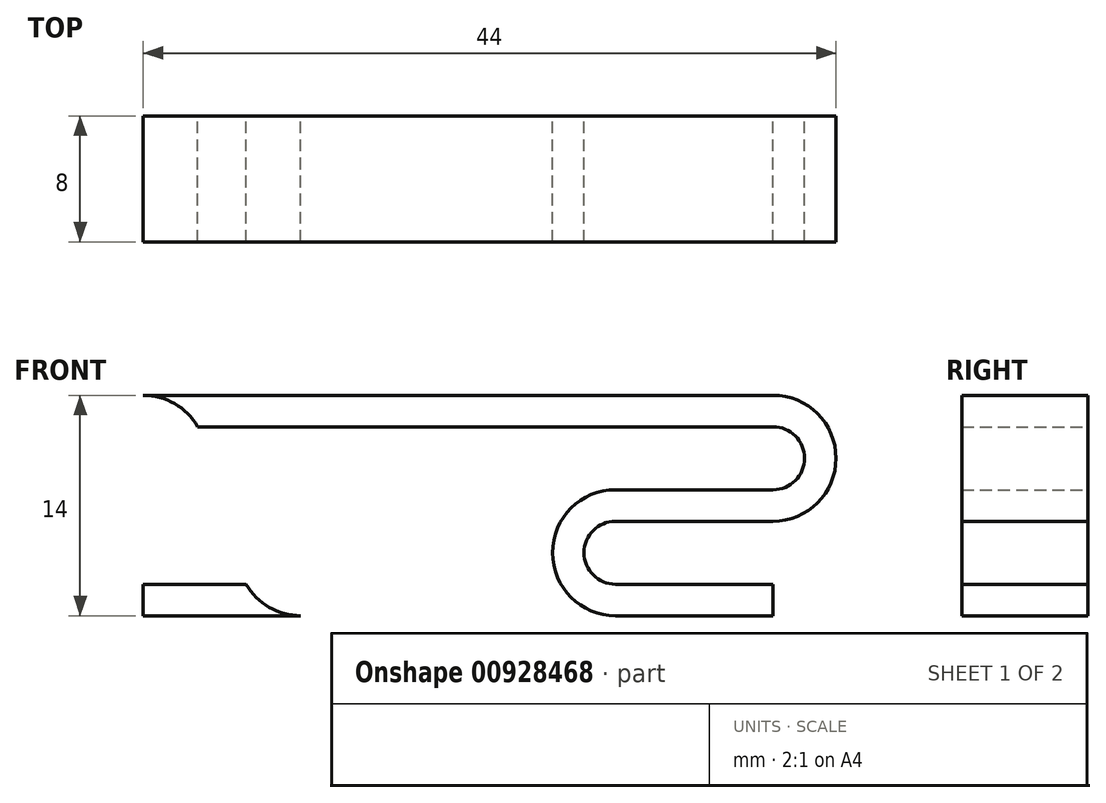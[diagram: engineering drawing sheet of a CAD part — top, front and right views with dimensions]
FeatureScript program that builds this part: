
annotation { "Feature Type Name" : "Feature", "Feature Type Description" : "" }
export const myFeature = defineFeature(function(context is Context, id is Id, definition is map)
    precondition{}
    {
        {
            var Q0;
            Q0=qCreatedBy(makeId("Front.planeOp"),FACE);
            var sketch = newSketch(context, id + "F0", { "sketchPlane" : qUnion([Q0])});
            skLineSegment(sketch, "E0", {"start": v(0, 0) * mm, "end": v(10, 0) * mm});
            skLineSegment(sketch, "E1", {"start": v(10, 0) * mm, "end": v(10, 2) * mm});
            skLineSegment(sketch, "E2", {"start": v(10, 2) * mm, "end": v(0, 2) * mm});
            skPoint(sketch, "E3", {"position": v(0, 4) * mm});
            skArc(sketch, "E4", {"start": v(0, 6) * mm, "mid": v(-2, 4) * mm, "end": v(0, 2) * mm});
            skLineSegment(sketch, "E5", {"start": v(0, 6) * mm, "end": v(10, 6) * mm});
            skPoint(sketch, "E6", {"position": v(10, 10) * mm});
            skArc(sketch, "E7", {"start": v(3.46, 6) * mm, "mid": v(-4, 4) * mm, "end": v(3.46, 2) * mm});
            skArc(sketch, "E8", {"start": v(6.54, 8) * mm, "mid": v(14, 10) * mm, "end": v(6.54, 12) * mm});
            skArc(sketch, "E9", {"start": v(10, 8) * mm, "mid": v(12, 10) * mm, "end": v(10, 12) * mm});
            skLineSegment(sketch, "E10", {"start": v(0, 8) * mm, "end": v(10, 8) * mm});
            skLineSegment(sketch, "E11", {"start": v(10, 12) * mm, "end": v(0, 12) * mm});
            skLineSegment(sketch, "E12", {"start": v(0, 12) * mm, "end": v(0, 14) * mm});
            skLineSegment(sketch, "E13", {"start": v(0, 14) * mm, "end": v(10, 14) * mm});
            skPoint(sketch, "E14", {"position": v(-4, 14) * mm});
            skPoint(sketch, "E14.positionSnap0", {"position": v(-4, 4) * mm});
            skPoint(sketch, "E15", {"position": v(-10, 14) * mm});
            skLineSegment(sketch, "E16", {"start": v(-10, 14) * mm, "end": v(-10, 0) * mm});
            skPoint(sketch, "E17.MirrorP", {"position": v(-16, 14) * mm});
            skPoint(sketch, "E18.MirrorP", {"position": v(-16, 4) * mm});
            skArc(sketch, "E19.MirrorCS", {"start": v(-23.46, 6) * mm, "mid": v(-16, 4) * mm, "end": v(-23.46, 2) * mm});
            skLineSegment(sketch, "E20.MirrorCS", {"start": v(-20, 6) * mm, "end": v(-30, 6) * mm});
            skArc(sketch, "E21.MirrorCS", {"start": v(-26.54, 8) * mm, "mid": v(-34, 10) * mm, "end": v(-26.54, 12) * mm});
            skArc(sketch, "E22.MirrorCS", {"start": v(-20, 6) * mm, "mid": v(-18, 4) * mm, "end": v(-20, 2) * mm});
            skLineSegment(sketch, "E23.MirrorCS", {"start": v(-20, 8) * mm, "end": v(-30, 8) * mm});
            skLineSegment(sketch, "E24.MirrorCS", {"start": v(-30, 0) * mm, "end": v(-30, 2) * mm});
            skLineSegment(sketch, "E25.MirrorCS", {"start": v(-30, 12) * mm, "end": v(-20, 12) * mm});
            skLineSegment(sketch, "E26.MirrorCS", {"start": v(-20, 14) * mm, "end": v(-30, 14) * mm});
            skArc(sketch, "E27.MirrorCS", {"start": v(-30, 8) * mm, "mid": v(-32, 10) * mm, "end": v(-30, 12) * mm});
            skLineSegment(sketch, "E28.MirrorCS", {"start": v(-30, 2) * mm, "end": v(-20, 2) * mm});
            skLineSegment(sketch, "E29.MirrorCS", {"start": v(-20, 0) * mm, "end": v(-30, 0) * mm});
            skLineSegment(sketch, "E30.MirrorCS", {"start": v(-20, 12) * mm, "end": v(-20, 14) * mm});
            skLineSegment(sketch, "E31", {"start": v(-20, 14) * mm, "end": v(0, 14) * mm});
            skLineSegment(sketch, "E32", {"start": v(0, 12) * mm, "end": v(-20, 12) * mm});
            skSolve(sketch);
        }
        {
            var Q0;
            {var subQ0=sQuery(id+"F0.wireOp",EDGE,"E8");var subQ1=sQuery(id+"F0.wireOp",EDGE,"E5");var subQ2=makeQuery(id+"F0.imprint","INTERSECT",VERTEX,{"derivedFrom":[subQ1,subQ0]});Q0=makeQuery(id+"F0.imprint","IMPRINT",FACE,{"disambiguationData":[TD([[makeQuery(id+"F0.imprint","IMPRINT",EDGE,{"disambiguationData":[TD([[subQ2,1.0]])],"derivedFrom":subQ1}),1.0]])]});}
            var Q1;
            {var subQ0=sQuery(id+"F0.wireOp",EDGE,"E9");Q1=makeQuery(id+"F0.imprint","IMPRINT",FACE,{"disambiguationData":[TD([[makeQuery(id+"F0.imprint","IMPRINT",EDGE,{"derivedFrom":subQ0}),-1.0]])]});}
            var Q2;
            {var subQ4=sQuery(id+"F0.wireOp",EDGE,"E12");Q2=makeQuery(id+"F0.imprint","IMPRINT",FACE,{"disambiguationData":[TD([[makeQuery(id+"F0.imprint","IMPRINT",EDGE,{"derivedFrom":subQ4}),-1.0]])]});}
            var Q3;
            {var subQ4=sQuery(id+"F0.wireOp",EDGE,"E4");Q3=makeQuery(id+"F0.imprint","IMPRINT",FACE,{"disambiguationData":[TD([[makeQuery(id+"F0.imprint","IMPRINT",EDGE,{"derivedFrom":subQ4}),-1.0]])]});}
            var Q4;
            {var subQ0=sQuery(id+"F0.wireOp",EDGE,"E0");Q4=makeQuery(id+"F0.imprint","IMPRINT",FACE,{"disambiguationData":[TD([[makeQuery(id+"F0.imprint","IMPRINT",EDGE,{"derivedFrom":subQ0}),1.0]])]});}
            var Q5;
            {var subQ0=sQuery(id+"F0.wireOp",EDGE,"E12");Q5=makeQuery(id+"F0.imprint","IMPRINT",FACE,{"disambiguationData":[TD([[makeQuery(id+"F0.imprint","IMPRINT",EDGE,{"derivedFrom":subQ0}),1.0]])]});}
            var Q6;
            {var subQ5=sQuery(id+"F0.wireOp",EDGE,"E30.MirrorCS");Q6=makeQuery(id+"F0.imprint","IMPRINT",FACE,{"disambiguationData":[TD([[makeQuery(id+"F0.imprint","IMPRINT",EDGE,{"derivedFrom":subQ5}),-1.0]])]});}
            var Q7;
            {var subQ3=sQuery(id+"F0.wireOp",EDGE,"E26.MirrorCS");Q7=makeQuery(id+"F0.imprint","IMPRINT",FACE,{"disambiguationData":[TD([[makeQuery(id+"F0.imprint","IMPRINT",EDGE,{"derivedFrom":subQ3}),1.0]])]});}
            var Q8;
            {var subQ7=sQuery(id+"F0.wireOp",EDGE,"E27.MirrorCS");Q8=makeQuery(id+"F0.imprint","IMPRINT",FACE,{"disambiguationData":[TD([[makeQuery(id+"F0.imprint","IMPRINT",EDGE,{"derivedFrom":subQ7}),1.0]])]});}
            var Q9;
            {var subQ0=sQuery(id+"F0.wireOp",EDGE,"E20.MirrorCS");var subQ1=sQuery(id+"F0.wireOp",EDGE,"E19.MirrorCS");var subQ2=makeQuery(id+"F0.imprint","INTERSECT",VERTEX,{"derivedFrom":[subQ1,subQ0]});Q9=makeQuery(id+"F0.imprint","IMPRINT",FACE,{"disambiguationData":[TD([[makeQuery(id+"F0.imprint","IMPRINT",EDGE,{"disambiguationData":[TD([[subQ2,-1.0]])],"derivedFrom":subQ1}),1.0]])]});}
            var Q10;
            {var subQ3=sQuery(id+"F0.wireOp",EDGE,"E22.MirrorCS");Q10=makeQuery(id+"F0.imprint","IMPRINT",FACE,{"disambiguationData":[TD([[makeQuery(id+"F0.imprint","IMPRINT",EDGE,{"derivedFrom":subQ3}),1.0]])]});}
            var Q11;
            {var subQ4=sQuery(id+"F0.wireOp",EDGE,"E24.MirrorCS");Q11=makeQuery(id+"F0.imprint","IMPRINT",FACE,{"disambiguationData":[TD([[makeQuery(id+"F0.imprint","IMPRINT",EDGE,{"derivedFrom":subQ4}),-1.0]])]});}
            extrude(context, id + "F1", {"entities" : qUnion([Q0, Q1, Q2, Q3, Q4, Q5, Q6, Q7, Q8, Q9, Q10, Q11]), "depth" : 8 * mm, "offsetDistance" : 25 * mm});
        }
    });
